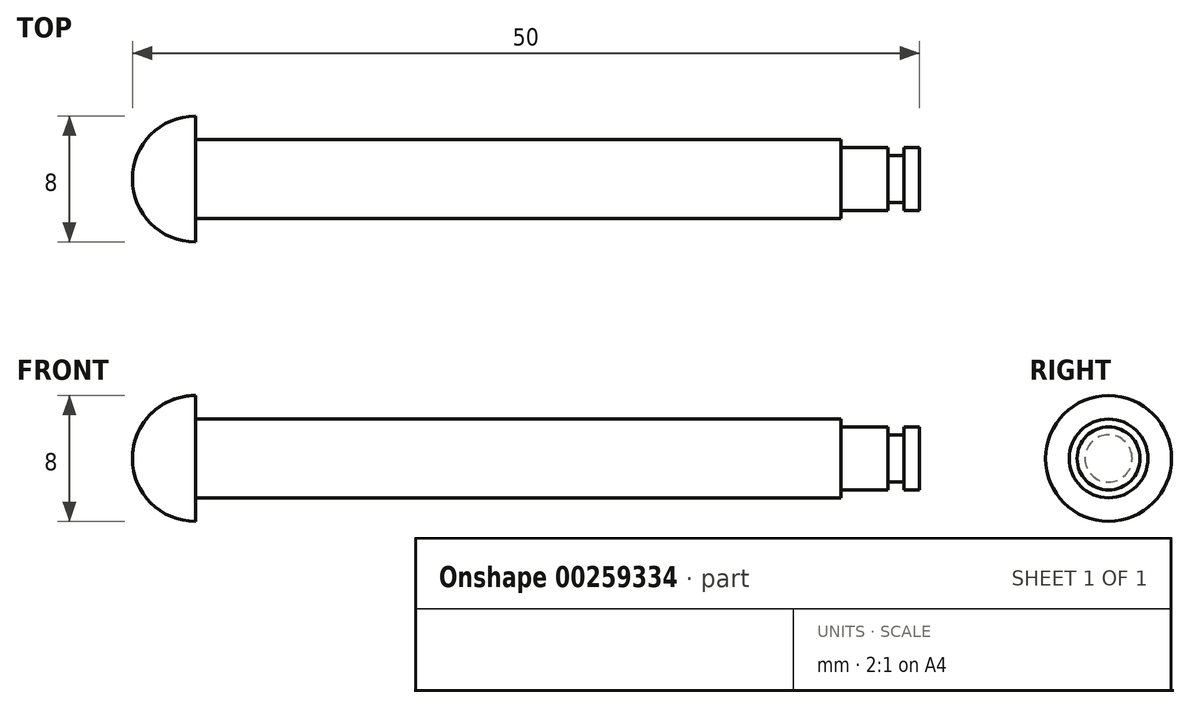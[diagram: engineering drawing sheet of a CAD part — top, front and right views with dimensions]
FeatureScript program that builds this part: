
annotation { "Feature Type Name" : "Feature", "Feature Type Description" : "" }
export const myFeature = defineFeature(function(context is Context, id is Id, definition is map)
    precondition{}
    {
        {
            var Q0;
            Q0=qCreatedBy(makeId("Front.planeOp"),FACE);
            var sketch = newSketch(context, id + "F0", { "sketchPlane" : qUnion([Q0])});
            skLineSegment(sketch, "E0", {"start": v(0, 2.5) * mm, "end": v(41, 2.5) * mm});
            skLineSegment(sketch, "E1", {"start": v(46, 2) * mm, "end": v(46, 0) * mm});
            skLineSegment(sketch, "E2", {"start": v(41, 2.5) * mm, "end": v(41, 2) * mm});
            skLineSegment(sketch, "E3", {"start": v(41, 2) * mm, "end": v(44, 2) * mm});
            skLineSegment(sketch, "E4", {"start": v(44, 2) * mm, "end": v(44, 1.5) * mm});
            skLineSegment(sketch, "E5", {"start": v(44, 1.5) * mm, "end": v(45, 1.5) * mm});
            skLineSegment(sketch, "E6", {"start": v(45, 1.5) * mm, "end": v(45, 2) * mm});
            skLineSegment(sketch, "E7", {"start": v(45, 2) * mm, "end": v(46, 2) * mm});
            skLineSegment(sketch, "E8", {"start": v(0, 2.5) * mm, "end": v(0, 4) * mm});
            skArc(sketch, "E9", {"start": v(0, 4) * mm, "mid": v(-2.83, 2.83) * mm, "end": v(-4, 0) * mm});
            skLineSegment(sketch, "E10", {"start": v(-4, 0) * mm, "end": v(46, 0) * mm, "construction": true});
            skLineSegment(sketch, "E11", {"start": v(-12, 0) * mm, "end": v(49.78, 0) * mm});
            skSolve(sketch);
        }
        {
            var Q0;
            Q0 = qSketchRegion(id + "F0", true);
            var Q1;
            Q1=sQuery(id+"F0.wireOp",EDGE,"E11");
            revolve(context, id + "F1", {"entities" : qUnion([Q0]), "axis" : qUnion([Q1]), "revolveType" : RevolveType.FULL});
        }
    });
